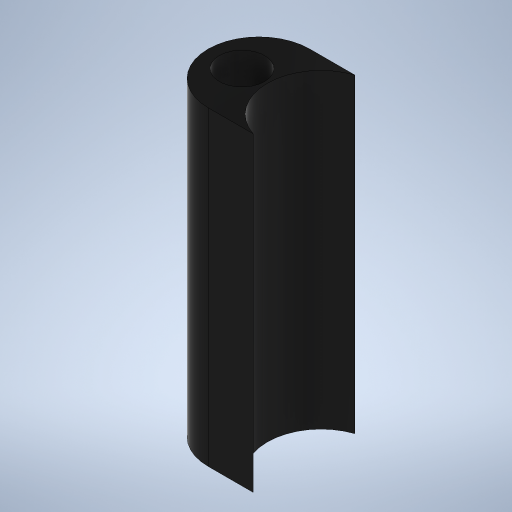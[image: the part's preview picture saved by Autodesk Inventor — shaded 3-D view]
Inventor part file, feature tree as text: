
AUTODESK INVENTOR PART (.ipt)
format: ipt  version: 2024 (Build 280153000, 153)  size: 271,360 bytes
history: native  units: mm
features: extrude x1, sketch x1
ambient origin geometry x8: Origin, YZ Plane, XZ Plane, XY Plane, X Axis, Y Axis, Z Axis, Center Point
bodies: Body1 (feature_tree)
feature tree (2):
  extrude  "Extrusion2"  [1 undecoded]
  sketch  "Skizze1"  dims[d2=55.0mm d3=0.0mm]
note: 1 required parameter value undecoded (feature->parameter linkage not recoverable at this tier; creation-order binding heuristic only, values carry confidence <= 0.55)
